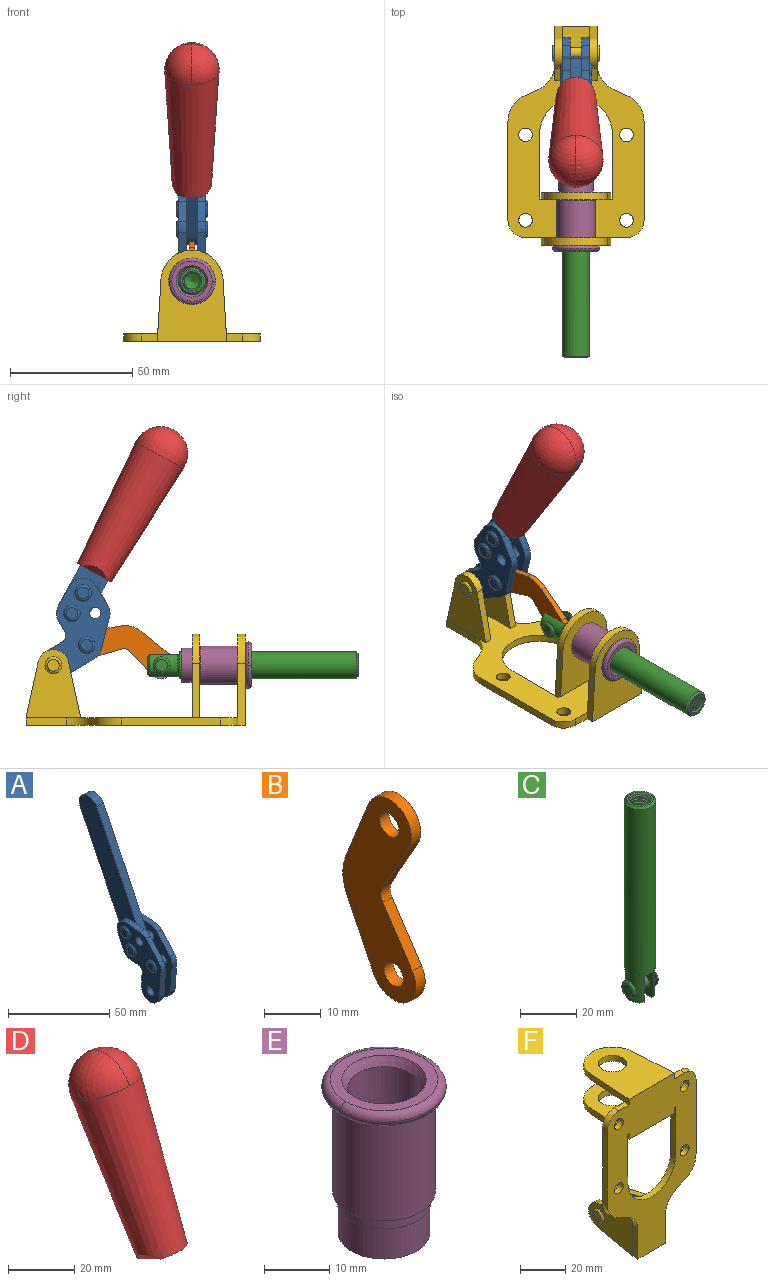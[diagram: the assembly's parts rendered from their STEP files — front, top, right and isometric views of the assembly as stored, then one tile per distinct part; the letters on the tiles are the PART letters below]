
ASSEMBLY  parts=6 mates=6
PART A: 59 faces, bbox 12.9x60.2x99.6 mm
  f0: torus R=2.39mm, axis (-1,0,0), area 14.9mm2, adj f20,f43,f51
  f1: torus R=2.39mm, axis (-1,0,0), area 14.9mm2, adj f19,f42,f51
  f2: torus R=2.39mm, axis (-1,0,0), area 14.9mm2, adj f18,f35,f51
  f3: torus R=2.39mm, axis (-1,0,0), area 14.9mm2, adj f14,f17,f23
  f4: torus R=2.39mm, axis (-1,0,0), area 14.9mm2, adj f13,f16,f23
  f5: torus R=2.39mm, axis (-1,0,0), area 14.9mm2, adj f12,f15,f23
  f6: cylinder r=2.39mm len=4.78mm, axis (1,0,0), area 46.5mm2, adj f48,f50,f51
  f7: cylinder r=2.39mm len=4.78mm, axis (1,0,0), area 46.5mm2, adj f50,f51
  f8: cylinder r=6.35mm len=12.68mm, axis (1,0,0), area 61.8mm2, adj f38,f39,f50,f51
  f9: cylinder r=2.39mm len=4.78mm, axis (-1,0,0), area 70.5mm2, adj f46,f50
  f10: cylinder r=2.39mm len=4.78mm, axis (-1,0,0), area 46.5mm2, adj f23,f45,f46
  f11: cylinder r=2.39mm len=4.78mm, axis (-1,0,0), area 46.5mm2, adj f23,f46
  f12: plane 4.78x4.78mm, normal (1,0,0), area 17.9mm2, adj f5,f15
  f13: plane 4.78x4.78mm, normal (1,0,0), area 17.9mm2, adj f4,f16
  f14: plane 4.78x4.78mm, normal (1,0,0), area 17.9mm2, adj f3,f17
  f15: torus R=2.39mm, axis (-1,0,0), area 14.9mm2, adj f5,f12,f23
  f16: torus R=2.39mm, axis (-1,0,0), area 14.9mm2, adj f4,f13,f23
  f17: torus R=2.39mm, axis (-1,0,0), area 14.9mm2, adj f3,f14,f23
  f18: plane 4.78x4.78mm, normal (-1,0,0), area 17.9mm2, adj f2,f35
  f19: plane 4.78x4.78mm, normal (-1,0,0), area 17.9mm2, adj f1,f42
  f20: plane 4.78x4.78mm, normal (-1,0,0), area 17.9mm2, adj f0,f43
  f21: plane 2.26x0.2mm, normal (1,0,0), area 0.2mm2, adj f31,f44
  f22: plane 2.26x0.2mm, normal (-1,0,0), area 0.2mm2, adj f41,f44
  f23: plane 39.37x30.77mm, normal (1,0,0), area 565.5mm2, adj f3,f4,f5,f10,f11,f15,f16,f17
  f24: cylinder r=6.1mm len=4.15mm, axis (-1,0,0), area 14.7mm2, adj f23,f25,f32,f46
  f25: plane 10.25x9.01mm, normal (0,-0.75,0.66), area 42.3mm2, adj f23,f24,f26,f46
  f26: cylinder r=6.35mm len=4.64mm, axis (-1,0,0), area 15.6mm2, adj f23,f25,f27,f46
  f27: plane 15.84x3.1mm, normal (0,-1,-0.07), area 49.2mm2, adj f23,f26,f28,f46
  f28: cylinder r=6.35mm len=12.68mm, axis (-1,0,0), area 61.8mm2, adj f23,f27,f29,f46
  f29: plane 8.11x3.1mm, normal (0,1,0.07), area 25.2mm2, adj f23,f28,f30,f46
  f30: cylinder r=3.05mm len=3.25mm, axis (-1,0,0), area 14.8mm2, adj f23,f29,f31,f46
  f31: plane 5.99x3.1mm, normal (0,0.07,-1), area 18.6mm2, adj f21,f23,f30,f44,f46
  f32: plane 9.5x3.1mm, normal (0,-0.07,1), area 29.5mm2, adj f23,f24,f33,f46,f47
  f33: cylinder r=6.1mm len=8.63mm, axis (-1,0,0), area 39.1mm2, adj f23,f32,f34,f47
  f34: plane 8.65x3.96mm, normal (0,0.91,-0.42), area 29.5mm2, adj f23,f33,f44,f47
  f35: torus R=2.39mm, axis (-1,0,0), area 14.9mm2, adj f2,f18,f51
  f36: plane 10.25x9.01mm, normal (0,-0.75,0.66), area 42.3mm2, adj f37,f49,f50,f51
  f37: cylinder r=6.35mm len=4.64mm, axis (1,0,0), area 15.6mm2, adj f36,f38,f50,f51
  f38: plane 15.84x3.1mm, normal (0,-1,-0.07), area 49.2mm2, adj f8,f37,f50,f51
  f39: plane 8.11x3.1mm, normal (0,1,0.07), area 25.2mm2, adj f8,f40,f50,f51
  f40: cylinder r=3.05mm len=3.25mm, axis (1,0,0), area 14.8mm2, adj f39,f41,f50,f51
  f41: plane 5.99x3.1mm, normal (0,0.07,-1), area 18.6mm2, adj f22,f40,f44,f50,f51
  f42: torus R=2.39mm, axis (-1,0,0), area 14.9mm2, adj f1,f19,f51
  f43: torus R=2.39mm, axis (-1,0,0), area 14.9mm2, adj f0,f20,f51
  f44: cylinder r=6.35mm len=12.12mm, axis (-1,0,0), area 128.9mm2, adj f21,f22,f23,f31,f34,f41,f46,f47
  f45: plane 2.65x1.35mm, normal (1,0,0), area 1mm2, adj f10,f55
  f46: plane 39.08x20.42mm, normal (-1,0,0), area 412.5mm2, adj f9,f10,f11,f24,f25,f26,f27,f28
  f47: plane 77.62x39.82mm, normal (1,0,0), area 850mm2, adj f32,f33,f34,f44,f53,f54,f55
  f48: plane 2.65x1.35mm, normal (-1,0,0), area 1mm2, adj f6,f55
  f49: cylinder r=6.1mm len=4.15mm, axis (1,0,0), area 14.7mm2, adj f36,f50,f51,f56
  f50: plane 39.08x20.42mm, normal (1,0,0), area 412.5mm2, adj f6,f7,f8,f9,f36,f37,f38,f39
  f51: plane 39.37x30.77mm, normal (-1,0,0), area 565.5mm2, adj f0,f1,f2,f6,f7,f8,f35,f36
  f52: plane 8.65x3.96mm, normal (0,0.91,-0.42), area 29.5mm2, adj f44,f51,f57,f58
  f53: plane 68.49x33.4mm, normal (0,0.9,-0.44), area 358.1mm2, adj f44,f47,f54,f58
  f54: cylinder r=6.35mm len=12.06mm, axis (1,0,0), area 93.7mm2, adj f47,f53,f55,f58
  f55: plane 68.49x33.4mm, normal (0,-0.9,0.44), area 358.1mm2, adj f44,f45,f46,f47,f48,f50,f54,f58
  f56: plane 9.5x3.1mm, normal (0,-0.07,1), area 29.5mm2, adj f49,f50,f51,f57,f58
  f57: cylinder r=6.1mm len=8.63mm, axis (1,0,0), area 39.1mm2, adj f51,f52,f56,f58
  f58: plane 77.62x39.82mm, normal (-1,0,0), area 850mm2, adj f44,f52,f53,f54,f55,f56,f57
PART B: 12 faces, bbox 2.3x18.2x42.8 mm
  f0: cylinder r=2.4mm len=4.8mm, axis (1,0,0), area 34.9mm2, adj f4,f11
  f1: cylinder r=10.41mm len=8.47mm, axis (1,0,0), area 20.2mm2, adj f4,f9,f10,f11
  f2: cylinder r=3.05mm len=3.16mm, axis (1,0,0), area 7.7mm2, adj f4,f6,f7,f11
  f3: cylinder r=2.4mm len=4.8mm, axis (1,0,0), area 34.9mm2, adj f4,f11
  f4: plane 42.81x18.23mm, normal (-1,0,0), area 414.1mm2, adj f0,f1,f2,f3,f5,f6,f7,f8
  f5: cylinder r=5.54mm len=10.67mm, axis (1,0,0), area 41.8mm2, adj f4,f6,f10,f11
  f6: plane 11.66x6.53mm, normal (0,-0.87,-0.49), area 30.9mm2, adj f2,f4,f5,f11
  f7: plane 11.17x7.33mm, normal (0,-0.84,0.55), area 30.9mm2, adj f2,f4,f8,f11
  f8: cylinder r=5.54mm len=10.51mm, axis (1,0,0), area 41.8mm2, adj f4,f7,f9,f11
  f9: plane 13.67x6.67mm, normal (0,0.9,-0.44), area 35.1mm2, adj f1,f4,f8,f11
  f10: plane 14.1x5.7mm, normal (0,0.93,0.37), area 35.1mm2, adj f1,f4,f5,f11
  f11: plane 42.81x18.23mm, normal (1,0,0), area 414.1mm2, adj f0,f1,f2,f3,f5,f6,f7,f8
PART C: 48 faces, bbox 12.6x11.1x86.1 mm
  f0: torus R=2.41mm, axis (-1,0,0), area 15mm2, adj f30,f32,f34
  f1: torus R=2.41mm, axis (-1,0,0), area 15mm2, adj f29,f31,f33
  f2: cylinder r=5.54mm len=72.39mm, axis (0,0,1), area 2518.5mm2, adj f3,f4,f42,f43
  f3: cone r=5.54mm half-angle=45deg, axis (0,0,1), area 7.6mm2, adj f2,f5,f41
  f4: cone r=5.54mm half-angle=45deg, axis (0,0,-1), area 34.9mm2, adj f2,f39
  f5: cylinder r=5.08mm len=11.48mm, axis (0,0,1), area 108.3mm2, adj f3,f7,f8,f41
  f6: cylinder r=2.41mm len=4.83mm, axis (-1,0,0), area 71.2mm2, adj f40,f41
  f7: cylinder r=2.41mm len=4.83mm, axis (-1,0,0), area 7.6mm2, adj f5,f34
  f8: cone r=5.08mm half-angle=45deg, axis (0,0,1), area 10.6mm2, adj f5,f37,f41
  f9: cone r=3.98mm half-angle=45deg, axis (0,0,1), area 17.6mm2, adj f27,f39,f45,f46,f47
  f10: cylinder r=2.41mm len=4.83mm, axis (-1,0,0), area 7.6mm2, adj f33,f38
  f11: cylinder r=3.2mm len=6.4mm, axis (0,0,1), area 78.4mm2, adj f12,f28,f44,f45,f47
  f12: cylinder r=3.2mm len=6.4mm, axis (0,0,1), area 10.5mm2, adj f11,f13,f45,f47
  f13: cylinder r=3.2mm len=6.4mm, axis (0,0,1), area 10.5mm2, adj f12,f14,f45,f47
  f14: cylinder r=3.2mm len=6.4mm, axis (0,0,1), area 10.5mm2, adj f13,f15,f45,f47
  f15: cylinder r=3.2mm len=6.4mm, axis (0,0,1), area 10.5mm2, adj f14,f16,f45,f47
  f16: cylinder r=3.2mm len=6.4mm, axis (0,0,1), area 10.5mm2, adj f15,f17,f45,f47
  f17: cylinder r=3.2mm len=6.4mm, axis (0,0,1), area 10.5mm2, adj f16,f18,f45,f47
  f18: cylinder r=3.2mm len=6.4mm, axis (0,0,1), area 10.5mm2, adj f17,f19,f45,f47
  f19: cylinder r=3.2mm len=6.4mm, axis (0,0,1), area 10.5mm2, adj f18,f20,f45,f47
  f20: cylinder r=3.2mm len=6.4mm, axis (0,0,1), area 10.5mm2, adj f19,f21,f45,f47
  f21: cylinder r=3.2mm len=6.4mm, axis (0,0,1), area 10.5mm2, adj f20,f22,f45,f47
  f22: cylinder r=3.2mm len=6.4mm, axis (0,0,1), area 10.5mm2, adj f21,f23,f45,f47
  f23: cylinder r=3.2mm len=6.4mm, axis (0,0,1), area 10.5mm2, adj f22,f24,f45,f47
  f24: cylinder r=3.2mm len=6.4mm, axis (0,0,1), area 10.5mm2, adj f23,f25,f45,f47
  f25: cylinder r=3.2mm len=6.4mm, axis (0,0,1), area 10.5mm2, adj f24,f26,f45,f47
  f26: cylinder r=3.2mm len=6.4mm, axis (0,0,1), area 10.5mm2, adj f25,f27,f45,f47
  f27: cylinder r=3.2mm len=6.4mm, axis (0,0,1), area 7.4mm2, adj f9,f26,f45,f47
  f28: cone r=3.2mm half-angle=60deg, axis (0,0,1), area 37.2mm2, adj f11
  f29: plane 4.83x4.83mm, normal (-1,0,0), area 18.3mm2, adj f1,f31
  f30: plane 4.83x4.83mm, normal (1,0,0), area 18.3mm2, adj f0,f32
  f31: torus R=2.41mm, axis (-1,0,0), area 15mm2, adj f1,f29,f33
  f32: torus R=2.41mm, axis (-1,0,0), area 15mm2, adj f0,f30,f34
  f33: plane 6.83x6.83mm, normal (1,0,0), area 18.3mm2, adj f1,f10,f31
  f34: plane 6.83x6.83mm, normal (-1,0,0), area 18.3mm2, adj f0,f7,f32
  f35: cone r=5.08mm half-angle=45deg, axis (0,0,1), area 10.6mm2, adj f36,f38,f40
  f36: plane 7.25x1.97mm, normal (0,0,-1), area 10mm2, adj f35,f40
  f37: plane 7.25x1.97mm, normal (0,0,-1), area 10mm2, adj f8,f41
  f38: cylinder r=5.08mm len=11.48mm, axis (0,0,1), area 108.3mm2, adj f10,f35,f40,f42
  f39: plane 9.55x9.55mm, normal (0,0,1), area 22mm2, adj f4,f9
  f40: plane 12.76x10.09mm, normal (1,0,0), area 95.7mm2, adj f6,f35,f36,f38,f42,f43
  f41: plane 12.76x10.09mm, normal (-1,0,0), area 95.7mm2, adj f3,f5,f6,f8,f37,f43
  f42: cone r=5.54mm half-angle=45deg, axis (0,0,1), area 7.6mm2, adj f2,f38,f40
  f43: plane 11.07x4.7mm, normal (0,0,-1), area 50.4mm2, adj f2,f40,f41
  f44: plane 0.89x0.62mm, normal (-1,0,0), area 0.3mm2, adj f11,f45,f46,f47
  f45: bspline ~24.8x7.63mm, area 266.6mm2, adj f9,f11,f12,f13,f14,f15,f16,f17
  f46: bspline ~24.87x7.63mm, area 73.6mm2, adj f9,f44,f45,f47
  f47: bspline ~24.98x7.63mm, area 272.5mm2, adj f9,f11,f12,f13,f14,f15,f16,f17
PART D: 11 faces, bbox 22.3x42.6x64.5 mm
  f0: sphere r=11.13mm, area 411.4mm2, adj f1,f8
  f1: cone r=11.11mm half-angle=3.3deg, axis (0,0.44,0.9), area 3251.8mm2, adj f0,f7,f8,f9,f10
  f2: cylinder r=6.16mm len=11.7mm, axis (1,0,0), area 89.5mm2, adj f3,f4,f5,f6
  f3: plane 60.23x36.75mm, normal (-1,0,0), area 763.6mm2, adj f2,f4,f6,f10
  f4: plane 51.37x25.05mm, normal (0,0.9,-0.44), area 264.2mm2, adj f2,f3,f5,f10
  f5: plane 60.23x36.75mm, normal (1,0,0), area 763.6mm2, adj f2,f4,f6,f10
  f6: plane 51.37x25.05mm, normal (0,-0.9,0.44), area 264.2mm2, adj f2,f3,f5,f10
  f7: plane 9.95x5.95mm, normal (0.71,-0.31,-0.64), area 25.8mm2, adj f1,f10
  f8: sphere r=11.13mm, area 411.4mm2, adj f0,f1
  f9: plane 9.95x5.95mm, normal (-0.71,-0.31,-0.64), area 25.8mm2, adj f1,f10
  f10: plane 14.27x11.38mm, normal (0,-0.44,-0.9), area 106.7mm2, adj f1,f3,f4,f5,f6,f7,f9
PART E: 15 faces, bbox 20.6x20.6x28.7 mm
  f0: torus R=8.26mm, axis (0,0,1), area 56.8mm2, adj f1,f10,f12
  f1: torus R=8.26mm, axis (0,0,1), area 56.8mm2, adj f0,f6,f13
  f2: cylinder r=5.59mm len=25.91mm, axis (0,0,1), area 909.6mm2, adj f3,f4
  f3: cone r=6.86mm half-angle=45deg, axis (0,0,-1), area 70.2mm2, adj f2,f14
  f4: cone r=6.47mm half-angle=30deg, axis (0,0,1), area 66.7mm2, adj f2,f13
  f5: cylinder r=7.04mm len=14.07mm, axis (0,0,1), area 252.6mm2, adj f11,f14
  f6: torus R=8.26mm, axis (0,0,1), area 56.8mm2, adj f1,f12,f13
  f7: cylinder r=7.16mm len=14.33mm, axis (0,0,1), area 91.5mm2, adj f9,f11
  f8: cylinder r=7.86mm len=18.42mm, axis (0,0,1), area 909.6mm2, adj f9,f10
  f9: plane 15.72x15.72mm, normal (0,0,-1), area 33mm2, adj f7,f8
  f10: plane 16.51x16.51mm, normal (0,0,-1), area 19.9mm2, adj f0,f8,f12
  f11: plane 14.33x14.33mm, normal (0,0,-1), area 5.7mm2, adj f5,f7
  f12: torus R=8.26mm, axis (0,0,1), area 56.8mm2, adj f0,f6,f10
  f13: plane 16.51x16.51mm, normal (0,0,1), area 82.7mm2, adj f1,f4,f6
  f14: plane 14.07x14.07mm, normal (0,0,-1), area 7.8mm2, adj f3,f5
PART F: 55 faces, bbox 55.7x37.4x89.8 mm
  f0: torus R=2.41mm, axis (-1,0,0), area 15mm2, adj f11,f15,f25
  f1: torus R=2.41mm, axis (-1,0,0), area 15mm2, adj f10,f12,f22
  f2: cylinder r=2.78mm len=5.56mm, axis (0,-1,0), area 54.2mm2, adj f30,f54
  f3: cylinder r=14.99mm len=29.97mm, axis (0,-1,0), area 145.9mm2, adj f30,f49,f53,f54
  f4: cylinder r=2.78mm len=5.56mm, axis (0,-1,0), area 54.2mm2, adj f30,f54
  f5: cylinder r=2.78mm len=5.56mm, axis (0,-1,0), area 54.2mm2, adj f30,f54
  f6: cylinder r=2.78mm len=5.56mm, axis (0,-1,0), area 54.2mm2, adj f30,f54
  f7: cylinder r=6.35mm len=12.7mm, axis (0,0,1), area 123.6mm2, adj f27,f51
  f8: cylinder r=6.35mm len=12.7mm, axis (0,0,-1), area 124.7mm2, adj f21,f35
  f9: cylinder r=2.41mm len=11.18mm, axis (-1,0,0), area 169.4mm2, adj f16,f19
  f10: plane 4.83x4.83mm, normal (1,0,0), area 18.3mm2, adj f1,f12
  f11: plane 4.83x4.83mm, normal (-1,0,0), area 18.3mm2, adj f0,f15
  f12: torus R=2.41mm, axis (-1,0,0), area 15mm2, adj f1,f10,f22
  f13: cylinder r=6.35mm len=12.41mm, axis (1,0,0), area 53.4mm2, adj f18,f19,f22,f23
  f14: cylinder r=6.35mm len=12.41mm, axis (-1,0,0), area 53.4mm2, adj f16,f17,f24,f25
  f15: torus R=2.41mm, axis (-1,0,0), area 15mm2, adj f0,f11,f25
  f16: plane 27.86x22.35mm, normal (1,0,0), area 425.4mm2, adj f9,f14,f17,f24,f30
  f17: plane 22.86x4.97mm, normal (0,0.21,0.98), area 72.5mm2, adj f14,f16,f25,f30
  f18: plane 22.86x4.97mm, normal (0,0.21,0.98), area 72.5mm2, adj f13,f19,f22,f30
  f19: plane 27.86x22.35mm, normal (-1,0,0), area 425.4mm2, adj f9,f13,f18,f23,f30
  f20: cylinder r=12.7mm len=25.35mm, axis (0,0,-1), area 119.8mm2, adj f21,f34,f35,f36
  f21: plane 34.21x28.07mm, normal (0,0,-1), area 702.4mm2, adj f8,f20,f30,f34,f36
  f22: plane 27.96x22.45mm, normal (1,0,0), area 407.2mm2, adj f1,f12,f13,f18,f23,f30,f42,f43
  f23: plane 22.86x4.97mm, normal (0,0.21,-0.98), area 72.5mm2, adj f13,f19,f22,f44
  f24: plane 22.86x4.97mm, normal (0,0.21,-0.98), area 72.5mm2, adj f14,f16,f25,f44
  f25: plane 27.86x22.35mm, normal (-1,0,0), area 407.1mm2, adj f0,f14,f15,f17,f24,f30,f45,f46
  f26: plane 3.1x0.95mm, normal (0,0,-1), area 2.7mm2, adj f30,f49,f50,f54
  f27: plane 34.21x28.07mm, normal (0,0,1), area 702.4mm2, adj f7,f28,f30,f50,f52
  f28: cylinder r=12.7mm len=25.35mm, axis (0,0,1), area 118.8mm2, adj f27,f50,f51,f52
  f29: plane 3.1x0.95mm, normal (0,0,-1), area 2.7mm2, adj f30,f52,f53,f54
  f30: plane 86.54x55.63mm, normal (0,1,0), area 2362.9mm2, adj f2,f3,f4,f5,f6,f16,f17,f18
  f31: plane 40.56x3.1mm, normal (-1,0,0), area 125.7mm2, adj f30,f32,f48,f54
  f32: cylinder r=7.11mm len=7.11mm, axis (0,-1,0), area 34.6mm2, adj f30,f31,f33,f54
  f33: plane 6.67x3.1mm, normal (0,0,1), area 20.4mm2, adj f30,f32,f34,f54
  f34: plane 25.39x3.13mm, normal (-1,0.06,0), area 79.5mm2, adj f20,f21,f33,f35,f54
  f35: plane 37.31x28.45mm, normal (0,0,1), area 789.9mm2, adj f8,f20,f34,f36,f54
  f36: plane 25.39x3.13mm, normal (1,0.06,0), area 79.5mm2, adj f20,f21,f35,f37,f54
  f37: plane 6.67x3.1mm, normal (0,0,1), area 20.4mm2, adj f30,f36,f38,f54
  f38: cylinder r=7.11mm len=7.11mm, axis (0,-1,0), area 34.6mm2, adj f30,f37,f39,f54
  f39: plane 40.56x3.1mm, normal (1,0,0), area 125.7mm2, adj f30,f38,f40,f54
  f40: cylinder r=11.18mm len=10.16mm, axis (0,-1,0), area 39.5mm2, adj f30,f39,f41,f54
  f41: plane 6.09x3.1mm, normal (0.42,0,-0.91), area 20.8mm2, adj f30,f40,f42,f54
  f42: cylinder r=11.18mm len=9.41mm, axis (0,-1,0), area 37.2mm2, adj f22,f30,f41,f43,f54
  f43: plane 16.5x3.1mm, normal (1,0,0), area 51.1mm2, adj f22,f42,f44,f54
  f44: plane 17.37x3.1mm, normal (0,0,-1), area 53.8mm2, adj f23,f24,f30,f43,f45,f54
  f45: plane 16.5x3.1mm, normal (-1,0,0), area 51.1mm2, adj f25,f44,f46,f54
  f46: cylinder r=11.18mm len=9.41mm, axis (0,-1,0), area 37.2mm2, adj f25,f30,f45,f47,f54
  f47: plane 6.09x3.1mm, normal (-0.42,0,-0.91), area 20.8mm2, adj f30,f46,f48,f54
  f48: cylinder r=11.18mm len=10.16mm, axis (0,-1,0), area 39.5mm2, adj f30,f31,f47,f54
  f49: plane 26.54x3.1mm, normal (-1,0,0), area 82.3mm2, adj f3,f26,f30,f54
  f50: plane 25.39x3.1mm, normal (1,0.06,0), area 78.8mm2, adj f26,f27,f28,f51,f54
  f51: plane 37.31x28.45mm, normal (0,0,-1), area 789.9mm2, adj f7,f28,f50,f52,f54
  f52: plane 25.39x3.1mm, normal (-1,0.06,0), area 78.8mm2, adj f27,f28,f29,f51,f54
  f53: plane 26.54x3.1mm, normal (1,0,0), area 82.3mm2, adj f3,f29,f30,f54
  f54: plane 89.66x55.63mm, normal (0,-1,0), area 2678.5mm2, adj f2,f3,f4,f5,f6,f26,f29,f31
PLACE A rot(axis=(1,0,0),55deg) t=(0,1.12,22.86)mm
PLACE B rot(axis=(1,0,0),106.9deg) t=(0,19.2,5.57)mm
PLACE C rot(axis=(1,0,0),90deg) t=(0,12.71,0)mm
PLACE D rot(axis=(1,0,0),55deg) t=(-0.04,1.12,22.86)mm
PLACE E rot(axis=(1,0,0),90deg) t=(0,9.43,0)mm
PLACE F rot(axis=(1,0,0),90deg) t=(0,9.43,0)mm fixed
MATE revolute B.f5 <-> C.f6  axis (1,0,0) through (0,-2.76,24.61)mm
MATE fastened F.f7 <-> E.f2  axis (0,-1,0) through (0,-36.96,24.61)mm
MATE fastened D.f2 <-> A.f54  axis (1,0,0) through (-2.35,-3,112.47)mm
MATE revolute B.f3 <-> A.f4  axis (1,0,0) through (0,27.92,32.79)mm
MATE revolute F.f0 <-> A.f7  axis (-1,0,0) through (0,41.52,24.61)mm
MATE slider C.f2 <-> E.f2  axis (0,-1,0) through (0,-46.07,24.61)mm
